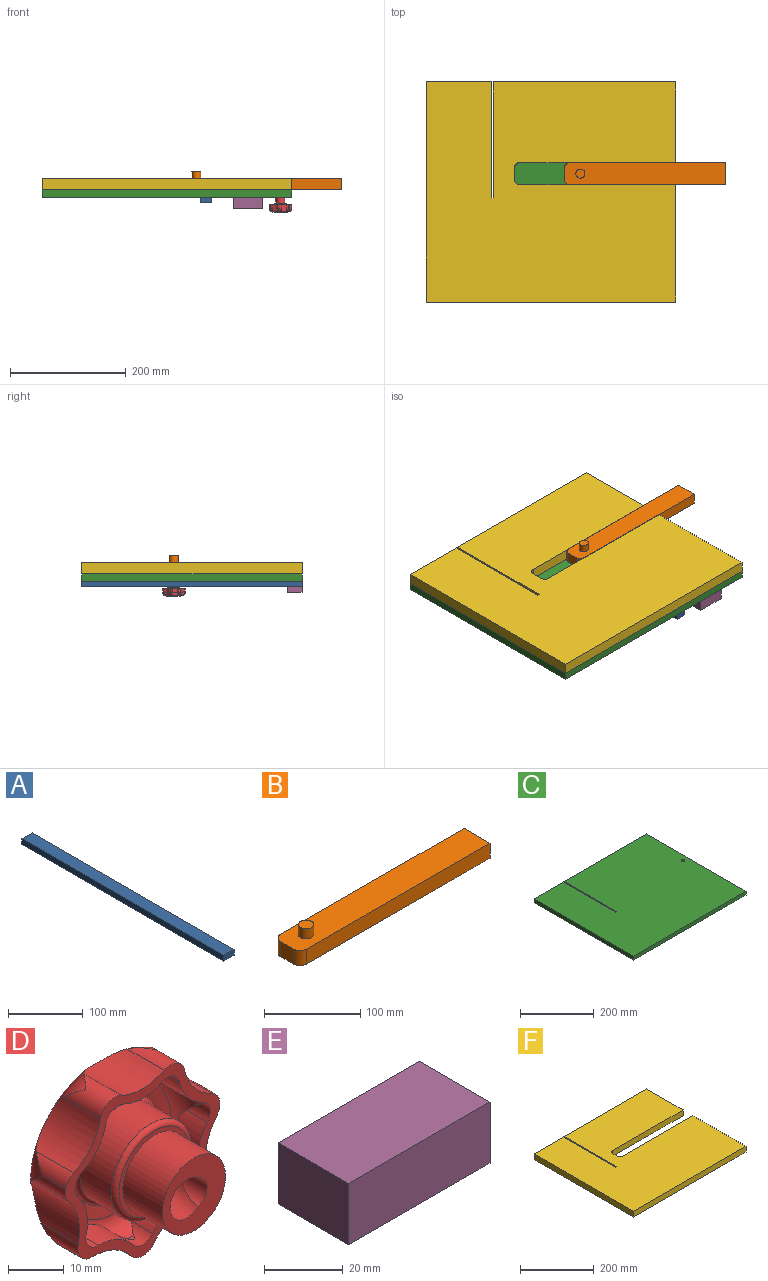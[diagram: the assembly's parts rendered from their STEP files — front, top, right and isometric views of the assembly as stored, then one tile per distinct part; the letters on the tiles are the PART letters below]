
ASSEMBLY  parts=6 mates=5
PART A: 6 faces, bbox 19.1x381x9.5 mm
  f0: plane 381x19.05mm, normal (0,0,1), area 7258.1mm2, adj f1,f3,f4,f5
  f1: plane 381x9.53mm, normal (-1,0,0), area 3629mm2, adj f0,f2,f4,f5
  f2: plane 381x19.05mm, normal (0,0,-1), area 7258.1mm2, adj f1,f3,f4,f5
  f3: plane 381x9.53mm, normal (1,0,0), area 3629mm2, adj f0,f2,f4,f5
  f4: plane 19.05x9.53mm, normal (0,1,0), area 181.5mm2, adj f0,f1,f2,f3
  f5: plane 19.05x9.53mm, normal (0,-1,0), area 181.5mm2, adj f0,f1,f2,f3
PART B: 14 faces, bbox 279.4x38.1x31.8 mm
  f0: plane 38.1x19.05mm, normal (1,0,0), area 544.4mm2, adj f1,f5,f6,f7,f8,f9,f10
  f1: plane 269.88x19.05mm, normal (0,1,0), area 5141.1mm2, adj f0,f2,f6,f7
  f2: cylinder r=9.53mm len=19.05mm, axis (0,0,-1), area 285mm2, adj f1,f3,f6,f7
  f3: plane 19.05x19.05mm, normal (-1,0,0), area 362.9mm2, adj f2,f4,f6,f7
  f4: cylinder r=9.53mm len=19.05mm, axis (0,0,-1), area 285mm2, adj f3,f5,f6,f7
  f5: plane 269.88x19.05mm, normal (0,-1,0), area 5141.1mm2, adj f0,f4,f6,f7
  f6: plane 279.4x38.1mm, normal (0,0,1), area 10408.3mm2, adj f0,f1,f2,f3,f4,f5,f12
  f7: plane 279.4x38.1mm, normal (0,0,-1), area 6735.2mm2, adj f0,f1,f2,f3,f4,f5,f8,f9
  f8: plane 203.2x9.53mm, normal (0,1,0), area 1935.5mm2, adj f0,f7,f10,f11
  f9: plane 203.2x9.53mm, normal (0,-1,0), area 1935.5mm2, adj f0,f7,f10,f11
  f10: plane 203.2x19.05mm, normal (0,0,-1), area 3871mm2, adj f0,f8,f9,f11
  f11: plane 19.05x9.53mm, normal (1,0,0), area 181.5mm2, adj f7,f8,f9,f10
  f12: cylinder r=7.94mm len=15.88mm, axis (0,0,-1), area 633.4mm2, adj f6,f13
  f13: plane 15.88x15.88mm, normal (0,0,1), area 197.9mm2, adj f12
PART C: 11 faces, bbox 431.8x381x12.7 mm
  f0: plane 315.91x12.7mm, normal (0,1,0), area 4012.1mm2, adj f1,f2,f5,f8
  f1: plane 431.8x381mm, normal (0,0,1), area 163807.9mm2, adj f0,f3,f4,f5,f6,f7,f8,f9
  f2: plane 431.8x381mm, normal (0,0,-1), area 163807.9mm2, adj f0,f3,f4,f5,f6,f7,f8,f9
  f3: plane 381x12.7mm, normal (-1,0,0), area 4838.7mm2, adj f1,f2,f4,f7
  f4: plane 431.8x12.7mm, normal (0,-1,0), area 5483.9mm2, adj f1,f2,f3,f5
  f5: plane 381x12.7mm, normal (1,0,0), area 4838.7mm2, adj f0,f1,f2,f4
  f6: cylinder r=4.76mm len=12.7mm, axis (0,0,-1), area 380mm2, adj f1,f2
  f7: plane 112.71x12.7mm, normal (0,1,0), area 1431.4mm2, adj f1,f2,f3,f9
  f8: plane 200.52x12.7mm, normal (-1,0,0), area 2546.7mm2, adj f0,f1,f2,f10
  f9: plane 200.52x12.7mm, normal (1,0,0), area 2546.7mm2, adj f1,f2,f7,f10
  f10: plane 12.7x3.18mm, normal (0,1,0), area 40.3mm2, adj f1,f2,f8,f9
PART D: 55 faces, bbox 44.3x28.1x44.3 mm
  f0: cylinder r=20mm len=5.22mm, axis (0,-1,0), area 0.2mm2, adj f3,f41
  f1: cylinder r=20mm len=5.22mm, axis (0,-1,0), area 0.1mm2, adj f3,f43
  f2: cylinder r=20mm len=5.22mm, axis (0,-1,0), area 0.1mm2, adj f3,f47
  f3: plane 39.18x38.38mm, normal (0,-1,0), area 242.8mm2, adj f0,f1,f2,f7,f8,f9,f10,f11
  f4: torus R=13.01mm, axis (0,-1,0), area 444.8mm2, adj f39,f41,f42,f43,f44,f45,f46,f47
  f5: cylinder r=3.32mm len=5.87mm, axis (0,-1,0), area 20.3mm2, adj f37,f40
  f6: cylinder r=3.32mm len=6.47mm, axis (0,-1,0), area 40.1mm2, adj f22,f40
  f7: cylinder r=3.18mm len=5.33mm, axis (0,-1,0), area 22.7mm2, adj f3,f8,f21,f35,f36
  f8: cylinder r=10.61mm len=9.32mm, axis (0,-1,0), area 61.5mm2, adj f3,f7,f9,f36
  f9: cylinder r=3.18mm len=5.33mm, axis (0,-1,0), area 22.7mm2, adj f3,f8,f10,f34,f36
  f10: cylinder r=10.61mm len=8.61mm, axis (0,-1,0), area 61.5mm2, adj f3,f9,f11,f36
  f11: cylinder r=3.18mm len=5.33mm, axis (0,-1,0), area 22.7mm2, adj f3,f10,f12,f33,f36
  f12: cylinder r=10.61mm len=8.61mm, axis (0,-1,0), area 61.5mm2, adj f3,f11,f13,f36
  f13: cylinder r=3.18mm len=5.33mm, axis (0,-1,0), area 22.7mm2, adj f3,f12,f14,f32,f36
  f14: cylinder r=10.61mm len=9.32mm, axis (0,-1,0), area 61.5mm2, adj f3,f13,f15,f36
  f15: cylinder r=3.18mm len=5.33mm, axis (0,-1,0), area 22.7mm2, adj f3,f14,f16,f31,f36
  f16: cylinder r=10.61mm len=7.47mm, axis (0,-1,0), area 61.5mm2, adj f3,f15,f17,f36
  f17: cylinder r=3.18mm len=5.33mm, axis (0,-1,0), area 22.7mm2, adj f3,f16,f18,f30,f36
  f18: cylinder r=10.61mm len=9.56mm, axis (0,-1,0), area 61.5mm2, adj f3,f17,f19,f36
  f19: cylinder r=3.18mm len=5.33mm, axis (0,-1,0), area 22.7mm2, adj f3,f18,f21,f29,f36
  f20: cylinder r=20mm len=5.22mm, axis (0,-1,0), area 0.2mm2, adj f3,f49
  f21: cylinder r=10.61mm len=7.47mm, axis (0,-1,0), area 61.5mm2, adj f3,f7,f19,f36
  f22: plane 16x16mm, normal (0,-1,0), area 140.4mm2, adj f6,f23,f40
  f23: cylinder r=8mm len=16mm, axis (0,-1,0), area 502.7mm2, adj f22,f24
  f24: plane 18x18mm, normal (0,-1,0), area 53.4mm2, adj f23,f25
  f25: torus R=9mm, axis (0,-1,0), area 95.1mm2, adj f24,f26
  f26: cylinder r=10mm len=20mm, axis (0,-1,0), area 496.9mm2, adj f25,f27
  f27: torus R=11mm, axis (0,-1,0), area 108.3mm2, adj f26,f28
  f28: cone r=13.8mm half-angle=85deg, axis (0,-1,0), area 212.8mm2, adj f27,f36
  f29: cone r=17.7mm half-angle=5deg, axis (0,-1,0), area 0.7mm2, adj f19,f36
  f30: cone r=17.7mm half-angle=5deg, axis (0,-1,0), area 0.7mm2, adj f17,f36
  f31: cone r=17.7mm half-angle=5deg, axis (0,-1,0), area 0.7mm2, adj f15,f36
  f32: cone r=17.7mm half-angle=5deg, axis (0,-1,0), area 0.7mm2, adj f13,f36
  f33: cone r=17.7mm half-angle=5deg, axis (0,-1,0), area 0.7mm2, adj f11,f36
  f34: cone r=17.7mm half-angle=5deg, axis (0,-1,0), area 0.7mm2, adj f9,f36
  f35: cone r=17.7mm half-angle=5deg, axis (0,-1,0), area 0.7mm2, adj f7,f36
  f36: torus R=13.45mm, axis (0,-1,0), area 246.1mm2, adj f7,f8,f9,f10,f11,f12,f13,f14
  f37: plane 14.95x14.95mm, normal (0,1,0), area 95.5mm2, adj f5,f38,f40
  f38: cylinder r=7mm len=14mm, axis (0,-1,0), area 110mm2, adj f37,f39
  f39: sphere r=113mm, area 555.9mm2, adj f4,f38
  f40: cylinder r=4.2mm len=25.64mm, axis (-0.14,-0.99,0), area 566.3mm2, adj f5,f6,f22,f37
  f41: cylinder r=3.64mm len=9.43mm, axis (0,-1,0), area 50.3mm2, adj f0,f3,f4,f42,f54
  f42: cylinder r=12.12mm len=11.46mm, axis (0,-1,0), area 123.2mm2, adj f3,f4,f41,f43
  f43: cylinder r=3.64mm len=9.44mm, axis (0,-1,0), area 50.3mm2, adj f1,f3,f4,f42,f44
  f44: cylinder r=12.12mm len=11.46mm, axis (0,-1,0), area 123.2mm2, adj f3,f4,f43,f45
  f45: cylinder r=3.64mm len=9.44mm, axis (0,-1,0), area 50.7mm2, adj f3,f4,f44,f46
  f46: cylinder r=12.12mm len=11.46mm, axis (0,-1,0), area 123.2mm2, adj f3,f4,f45,f47
  f47: cylinder r=3.64mm len=9.44mm, axis (0,-1,0), area 50.3mm2, adj f2,f3,f4,f46,f48
  f48: cylinder r=12.12mm len=11.46mm, axis (0,-1,0), area 123.2mm2, adj f3,f4,f47,f49
  f49: cylinder r=3.64mm len=9.43mm, axis (0,-1,0), area 50.3mm2, adj f3,f4,f20,f48,f50
  f50: cylinder r=12.12mm len=11.46mm, axis (0,-1,0), area 123.2mm2, adj f3,f4,f49,f51
  f51: cylinder r=3.64mm len=9.43mm, axis (0,-1,0), area 50.4mm2, adj f3,f4,f50,f52
  f52: cylinder r=12.12mm len=11.46mm, axis (0,-1,0), area 123.2mm2, adj f3,f4,f51,f53
  f53: cylinder r=3.64mm len=9.43mm, axis (0,-1,0), area 50.4mm2, adj f3,f4,f52,f54
  f54: cylinder r=12.12mm len=11.46mm, axis (0,-1,0), area 123.2mm2, adj f3,f4,f41,f53
PART E: 6 faces, bbox 50.8x25.4x19.1 mm
  f0: plane 25.4x19.05mm, normal (-1,0,0), area 483.9mm2, adj f1,f3,f4,f5
  f1: plane 50.8x19.05mm, normal (0,-1,0), area 967.7mm2, adj f0,f2,f4,f5
  f2: plane 25.4x19.05mm, normal (1,0,0), area 483.9mm2, adj f1,f3,f4,f5
  f3: plane 50.8x19.05mm, normal (0,1,0), area 967.7mm2, adj f0,f2,f4,f5
  f4: plane 50.8x25.4mm, normal (0,0,-1), area 1290.3mm2, adj f0,f1,f2,f3
  f5: plane 50.8x25.4mm, normal (0,0,1), area 1290.3mm2, adj f0,f1,f2,f3
PART F: 16 faces, bbox 431.8x381x19.1 mm
  f0: plane 315.91x19.05mm, normal (0,1,0), area 6018.1mm2, adj f1,f2,f7,f13
  f1: plane 431.8x381mm, normal (0,0,1), area 153272.9mm2, adj f0,f3,f4,f5,f6,f7,f8,f9
  f2: plane 431.8x381mm, normal (0,0,-1), area 153272.9mm2, adj f0,f3,f4,f5,f6,f7,f8,f9
  f3: plane 203.2x19.05mm, normal (1,0,0), area 3871mm2, adj f1,f2,f6,f12
  f4: plane 112.71x19.05mm, normal (0,1,0), area 2147.2mm2, adj f1,f2,f5,f14
  f5: plane 381x19.05mm, normal (-1,0,0), area 7258mm2, adj f1,f2,f4,f6
  f6: plane 431.8x19.05mm, normal (0,-1,0), area 8225.8mm2, adj f1,f2,f3,f5
  f7: plane 139.7x19.05mm, normal (1,0,0), area 2661.3mm2, adj f0,f1,f2,f8
  f8: plane 269.88x19.05mm, normal (0,-1,0), area 5141.1mm2, adj f1,f2,f7,f9
  f9: cylinder r=9.53mm len=19.05mm, axis (0,0,1), area 285mm2, adj f1,f2,f8,f10
  f10: plane 19.05x19.05mm, normal (1,0,0), area 362.9mm2, adj f1,f2,f9,f11
  f11: cylinder r=9.53mm len=19.05mm, axis (0,0,1), area 285mm2, adj f1,f2,f10,f12
  f12: plane 269.88x19.05mm, normal (0,1,0), area 5141.1mm2, adj f1,f2,f3,f11
  f13: plane 200.52x19.05mm, normal (-1,0,0), area 3820mm2, adj f0,f1,f2,f15
  f14: plane 200.52x19.05mm, normal (1,0,0), area 3820mm2, adj f1,f2,f4,f15
  f15: plane 19.05x3.18mm, normal (0,1,0), area 60.5mm2, adj f1,f2,f13,f14
PLACE A t=(68.88,-27.5,51.74)mm
PLACE B t=(-297.09,-0.65,51.74)mm
PLACE C t=(-383.59,-0.65,51.74)mm
PLACE D rot(axis=(-1,0.04,-0.04),90.1deg) t=(366.69,-2.05,51.74)mm
PLACE E t=(-386.31,-0.65,51.74)mm
PLACE F t=(-383.59,-0.65,51.74)mm
MATE fastened A.f0 <-> C.f2  axis (0,0,1) through (246.68,-224.35,51.74)mm
MATE fastened F.f2 <-> C.f1  axis (0,0,-1) through (386.38,-224.35,64.44)mm
MATE fastened E.f5 <-> C.f2  axis (0,0,1) through (335.58,-224.35,51.74)mm
MATE revolute D.f22 <-> C.f6  axis (0,0,1) through (367.33,-2.1,51.74)mm
MATE slider F.f3 <-> B.f0  axis (1,0,0) through (386.38,-21.15,73.97)mm
